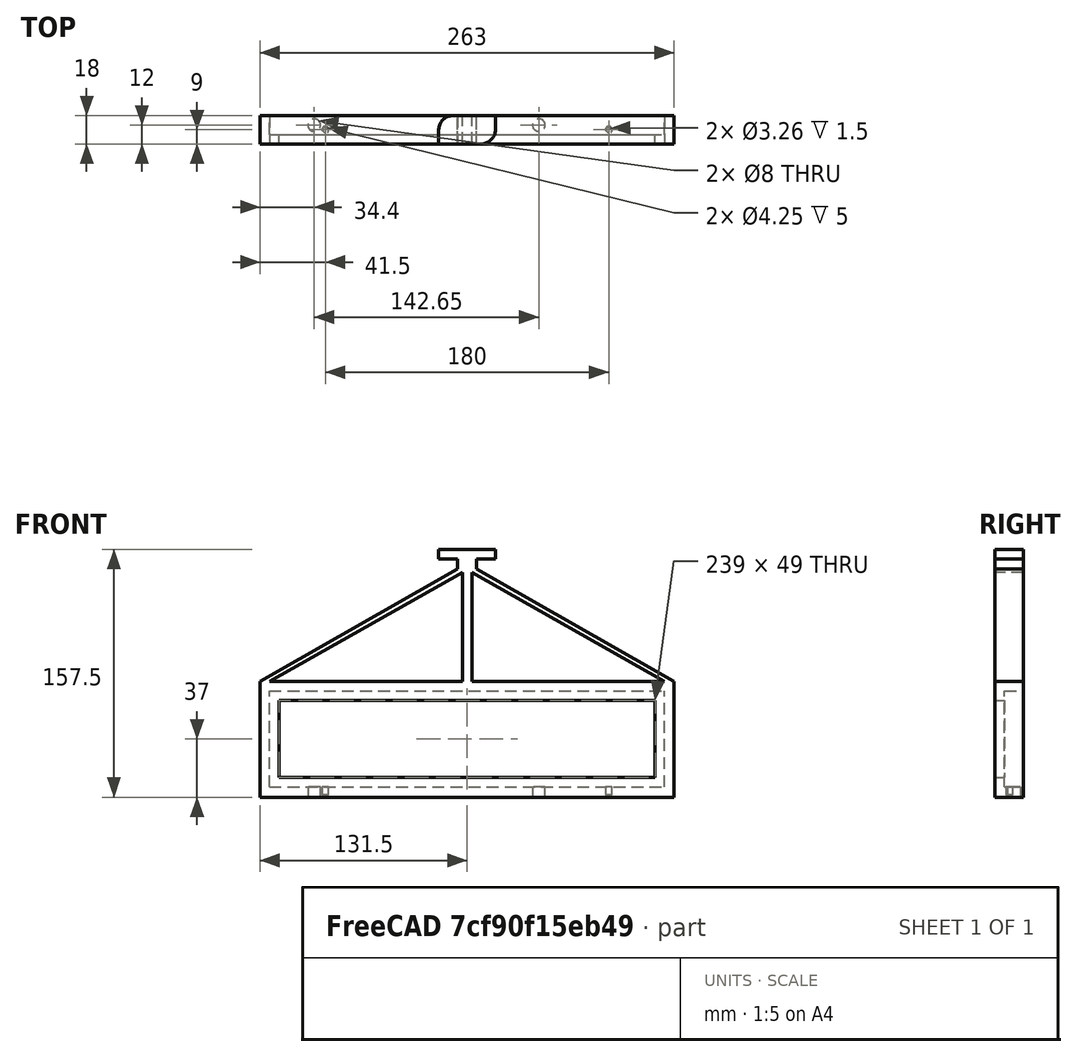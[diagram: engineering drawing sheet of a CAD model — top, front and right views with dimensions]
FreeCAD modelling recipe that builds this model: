
FCSTD DOCUMENT  (FreeCAD 0.20R2887)
Label: HiCoHolderPt2
License: All rights reserved
LicenseURL: http://en.wikipedia.org/wiki/All_rights_reserved
objects: Part::Cylinder×8, Part::Box×7, Part::MultiFuse×3, Part::Wedge×2, Part::Cut×1
note: 21 computed .brp shape members not serialized (recipe doc carries the construction recipe); baked Part::Feature solids carry a one-line shape summary decoded from their .brp

FEATURE [Part::Cylinder] Cylinder002
  Angle = 360
  AttacherType = Attacher::AttachEngine3D
  FirstAngle = 0
  Height = 8
  Placement = pos=(34.4,12,-0.5) rot=(0,0,1;0rad)
  Radius = 4
  SecondAngle = 0
FEATURE [Part::Cylinder] Cylinder003
  Angle = 360
  AttacherType = Attacher::AttachEngine3D
  FirstAngle = 0
  Height = 8
  Placement = pos=(177.05,12,-0.5) rot=(0,0,1;0rad)
  Radius = 4
  SecondAngle = 0
FEATURE [Part::Cylinder] Cylinder004
  Angle = 360
  AttacherType = Attacher::AttachEngine3D
  FirstAngle = 0
  Height = 10
  Placement = pos=(41.5,9,-0.5) rot=(0,0,1;0rad)
  Radius = 1.63
  SecondAngle = 0
  expr: .Placement.Base.x = 131.5 - 90
FEATURE [Part::Cylinder] Cylinder005
  Angle = 360
  AttacherType = Attacher::AttachEngine3D
  FirstAngle = 0
  Height = 10
  Placement = pos=(221.5,9,-0.5) rot=(0,0,1;0rad)
  Radius = 1.63
  SecondAngle = 0
  expr: .Placement.Base.x = 131.5 + 90
FEATURE [Part::Cylinder] Cylinder006
  Angle = 360
  AttacherType = Attacher::AttachEngine3D
  FirstAngle = 0
  Height = 5
  Placement = pos=(41.5,9,1) rot=(0,0,1;0rad)
  Radius = 2.125
  SecondAngle = 0
  expr: .Placement.Base.x = 131.5 - 90
FEATURE [Part::Cylinder] Cylinder007
  Angle = 360
  AttacherType = Attacher::AttachEngine3D
  FirstAngle = 0
  Height = 5
  Placement = pos=(221.5,9,1) rot=(0,0,1;0rad)
  Radius = 2.125
  SecondAngle = 0
  expr: .Placement.Base.x = 131.5 + 90
FEATURE [Part::Box] Box007  label="Cube007"
  AttacherType = Attacher::AttachEngine3D
  Height = 73.5
  Length = 263
  Placement = pos=(0,0,-0.5) rot=(0,0,1;0rad)
  Width = 18
FEATURE [Part::Box] Box008  label="Cube008"
  AttacherType = Attacher::AttachEngine3D
  Height = 61
  Length = 251
  Placement = pos=(6,6,6) rot=(0,0,1;0rad)
  Width = 12
FEATURE [Part::Box] Box009  label="Cube009"
  AttacherType = Attacher::AttachEngine3D
  Height = 49
  Length = 239
  Placement = pos=(12,0,12) rot=(0,0,1;0rad)
  Width = 12
FEATURE [Part::Wedge] Wedge002
  AttacherType = Attacher::AttachEngine3D
  Placement = pos=(0,18,73) rot=(1,0,0;1.5708rad)
  X2max = 131.5
  X2min = 131.5
  Xmax = 263
  Xmin = 0
  Ymax = 75
  Ymin = 0
  Z2max = 18
  Z2min = 0
  Zmax = 18
  Zmin = 0
FEATURE [Part::MultiFuse] Fusion003  label="Material001"
  Shapes = -> [Box007,Wedge002]
FEATURE [Part::Wedge] Wedge003
  AttacherType = Attacher::AttachEngine3D
  Placement = pos=(0,18,73) rot=(1,0,0;1.5708rad)
  X2max = 131.5
  X2min = 131.5
  Xmax = 257
  Xmin = 6
  Ymax = 71
  Ymin = 0
  Z2max = 18
  Z2min = 0
  Zmax = 18
  Zmin = 0
FEATURE [Part::MultiFuse] Fusion002  label="Holes001"
  Shapes = -> [Wedge003,Box008,Box009,Cylinder003,Cylinder004,Cylinder005,Cylinder006,Cylinder007,Cylinder002]
FEATURE [Part::Cut] Cut001
  Base = -> Fusion003
  Tool = -> Fusion002
FEATURE [Part::Box] Box003  label="Cube003"
  AttacherType = Attacher::AttachEngine3D
  Height = 75
  Length = 6
  Placement = pos=(128.5,0,73) rot=(0,0,1;0rad)
  Width = 18
FEATURE [Part::Box] Box004  label="Cube004"
  AttacherType = Attacher::AttachEngine3D
  Height = 6
  Length = 27
  Placement = pos=(113.5,0,151) rot=(0,0,1;0rad)
  Width = 9
  expr: .Placement.Base.x = 131.5 - 18
FEATURE [Part::Box] Box005  label="Cube005"
  AttacherType = Attacher::AttachEngine3D
  Height = 6
  Length = 27
  Placement = pos=(122.5,9,151) rot=(0,0,1;0rad)
  Width = 9
  expr: .Placement.Base.x = 131.5 - 13 + 4
FEATURE [Part::Cylinder] Cylinder
  Angle = 360
  AttacherType = Attacher::AttachEngine3D
  FirstAngle = 0
  Height = 6
  Placement = pos=(140.5,9,151) rot=(0,0,1;0rad)
  Radius = 9
  SecondAngle = 0
  expr: .Placement.Base.x = 131.5 + 9
FEATURE [Part::Cylinder] Cylinder001
  Angle = 360
  AttacherType = Attacher::AttachEngine3D
  FirstAngle = 0
  Height = 6
  Placement = pos=(122.5,9,151) rot=(0,0,1;0rad)
  Radius = 9
  SecondAngle = 0
  expr: .Placement.Base.x = 131.5 - 9
FEATURE [Part::Box] Box006  label="Cube006"
  AttacherType = Attacher::AttachEngine3D
  Height = 6.43
  Length = 12
  Placement = pos=(125.5,0,144.57) rot=(0,0,1;0rad)
  Width = 18
FEATURE [Part::MultiFuse] Fusion
  Shapes = -> [Cut001,Box003,Box004,Box005,Cylinder,Cylinder001,Box006]
